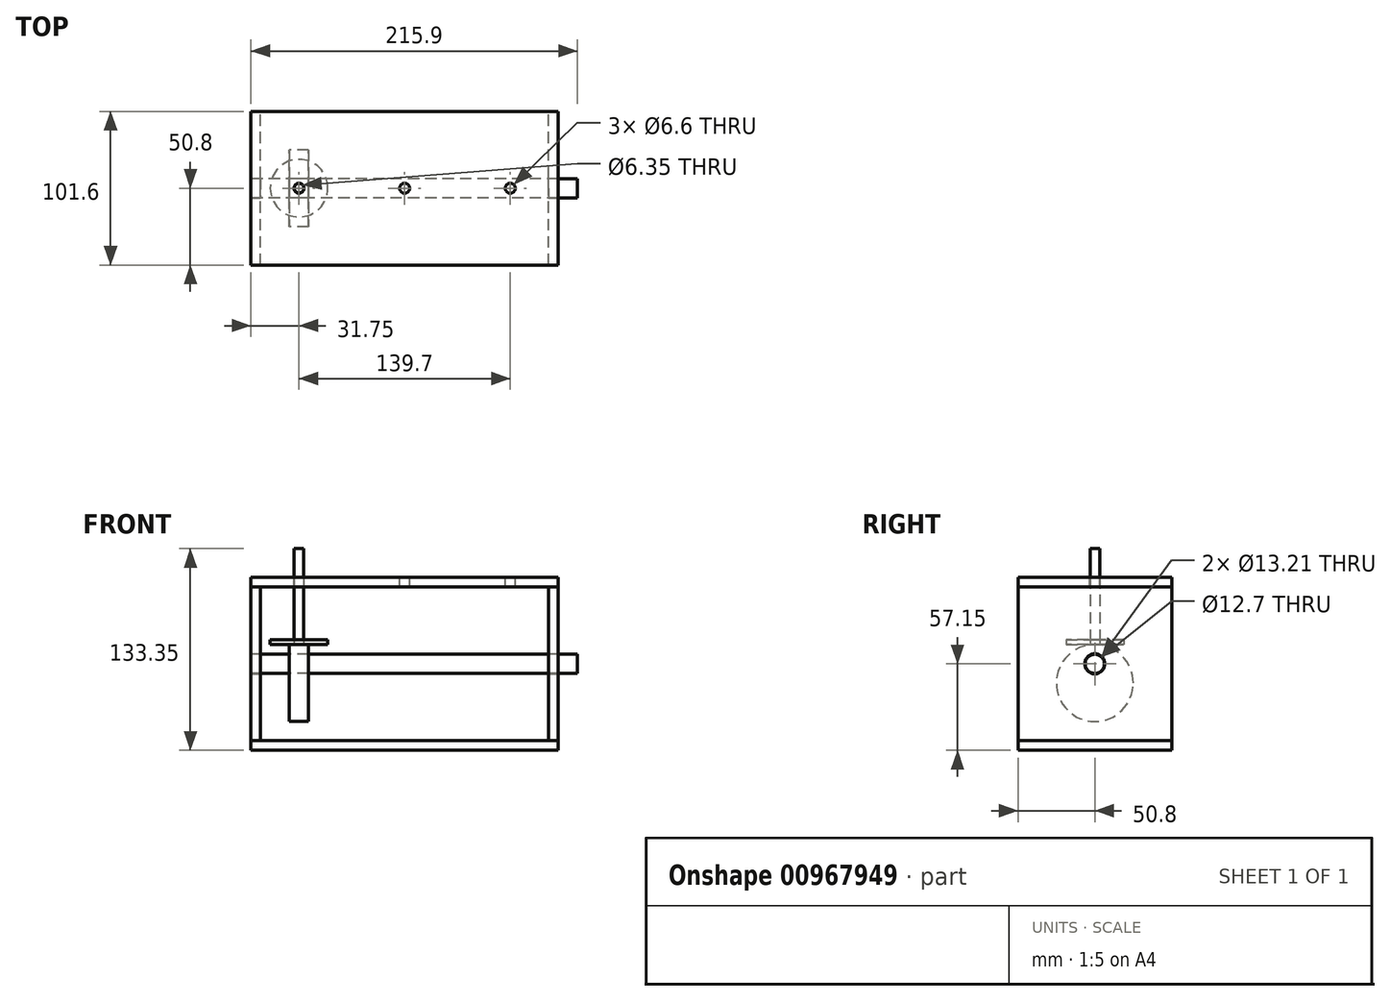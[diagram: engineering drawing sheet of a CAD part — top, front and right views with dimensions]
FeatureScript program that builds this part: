
annotation { "Feature Type Name" : "Feature", "Feature Type Description" : "" }
export const myFeature = defineFeature(function(context is Context, id is Id, definition is map)
    precondition{}
    {
        {
            assignVariable(context, id + "F0", {"name" : "thickness", "anyValue" : 101.6 * mm});
        }
        {
            var Q0;
            Q0=qCreatedBy(makeId("Front.planeOp"),FACE);
            var sketch = newSketch(context, id + "F1", { "sketchPlane" : qUnion([Q0])});
            skLineSegment(sketch, "E0.bottom", {"start": v(-101.6, 6.35) * mm, "end": v(101.6, 6.35) * mm});
            skLineSegment(sketch, "E0.top", {"start": v(-101.6, 0) * mm, "end": v(101.6, 0) * mm});
            skLineSegment(sketch, "E0.left", {"start": v(-101.6, 6.35) * mm, "end": v(-101.6, 0) * mm});
            skLineSegment(sketch, "E0.right", {"start": v(101.6, 6.35) * mm, "end": v(101.6, 0) * mm});
            skLineSegment(sketch, "E1", {"start": v(-101.6, 6.35) * mm, "end": v(-101.6, 107.95) * mm});
            skLineSegment(sketch, "E2", {"start": v(-101.6, 107.95) * mm, "end": v(101.6, 107.95) * mm});
            skLineSegment(sketch, "E3", {"start": v(101.6, 107.95) * mm, "end": v(101.6, 6.35) * mm});
            skLineSegment(sketch, "E4", {"start": v(-95.25, 6.35) * mm, "end": v(-95.25, 107.95) * mm});
            skLineSegment(sketch, "E5", {"start": v(95.25, 6.35) * mm, "end": v(95.25, 107.95) * mm});
            skLineSegment(sketch, "E6", {"start": v(-95.25, 57.15) * mm, "end": v(-101.6, 57.15) * mm, "construction": true});
            skLineSegment(sketch, "E7", {"start": v(95.25, 57.15) * mm, "end": v(101.6, 57.15) * mm, "construction": true});
            skLineSegment(sketch, "E8", {"start": v(-101.6, 107.95) * mm, "end": v(-101.6, 114.3) * mm});
            skLineSegment(sketch, "E9", {"start": v(-101.6, 114.3) * mm, "end": v(101.6, 114.3) * mm});
            skLineSegment(sketch, "E10", {"start": v(101.6, 114.3) * mm, "end": v(101.6, 107.95) * mm});
            skLineSegment(sketch, "E11", {"start": v(-95.25, 57.15) * mm, "end": v(-69.85, 57.15) * mm});
            skLineSegment(sketch, "E12", {"start": v(-69.85, 57.15) * mm, "end": v(0, 57.15) * mm});
            skLineSegment(sketch, "E13", {"start": v(0, 57.15) * mm, "end": v(69.85, 57.15) * mm});
            skLineSegment(sketch, "E14", {"start": v(69.85, 57.15) * mm, "end": v(95.25, 57.15) * mm});
            skLineSegment(sketch, "E15", {"start": v(-69.85, 57.15) * mm, "end": v(-69.85, 44.45) * mm, "construction": true});
            skLineSegment(sketch, "E16", {"start": v(0, 63.5) * mm, "end": v(0, 57.15) * mm, "construction": true});
            skLineSegment(sketch, "E17", {"start": v(69.85, 57.15) * mm, "end": v(69.85, 63.5) * mm, "construction": true});
            skLineSegment(sketch, "E18.bottom", {"start": v(-63.5, 69.85) * mm, "end": v(-76.2, 69.85) * mm});
            skLineSegment(sketch, "E18.top", {"start": v(-63.5, 19.05) * mm, "end": v(-76.2, 19.05) * mm});
            skLineSegment(sketch, "E18.left", {"start": v(-63.5, 69.85) * mm, "end": v(-63.5, 19.05) * mm});
            skLineSegment(sketch, "E18.right", {"start": v(-76.2, 69.85) * mm, "end": v(-76.2, 19.05) * mm});
            skPoint(sketch, "E18.middle", {"position": v(-69.85, 44.45) * mm});
            skLineSegment(sketch, "E19.bottom", {"start": v(6.35, 38.1) * mm, "end": v(-6.35, 38.1) * mm});
            skLineSegment(sketch, "E19.top", {"start": v(6.35, 88.9) * mm, "end": v(-6.35, 88.9) * mm});
            skLineSegment(sketch, "E19.left", {"start": v(6.35, 38.1) * mm, "end": v(6.35, 88.9) * mm});
            skLineSegment(sketch, "E19.right", {"start": v(-6.35, 38.1) * mm, "end": v(-6.35, 88.9) * mm});
            skPoint(sketch, "E19.middle", {"position": v(0, 63.5) * mm});
            skLineSegment(sketch, "E20.bottom", {"start": v(63.5, 38.1) * mm, "end": v(76.2, 38.1) * mm});
            skLineSegment(sketch, "E20.top", {"start": v(63.5, 88.9) * mm, "end": v(76.2, 88.9) * mm});
            skLineSegment(sketch, "E20.left", {"start": v(63.5, 38.1) * mm, "end": v(63.5, 88.9) * mm});
            skLineSegment(sketch, "E20.right", {"start": v(76.2, 38.1) * mm, "end": v(76.2, 88.9) * mm});
            skPoint(sketch, "E20.middle", {"position": v(69.85, 63.5) * mm});
            skLineSegment(sketch, "E21", {"start": v(-76.2, 44.45) * mm, "end": v(-63.5, 44.45) * mm});
            skLineSegment(sketch, "E22", {"start": v(-6.35, 63.5) * mm, "end": v(6.35, 63.5) * mm});
            skLineSegment(sketch, "E23", {"start": v(63.5, 63.5) * mm, "end": v(76.2, 63.5) * mm});
            skLineSegment(sketch, "E24", {"start": v(-69.85, 69.85) * mm, "end": v(-69.85, 133.35) * mm, "construction": true});
            skLineSegment(sketch, "E25", {"start": v(0, 88.9) * mm, "end": v(0, 152.4) * mm, "construction": true});
            skLineSegment(sketch, "E26", {"start": v(69.85, 88.9) * mm, "end": v(69.85, 152.4) * mm, "construction": true});
            skSolve(sketch);
        }
        {
            var Q0;
            Q0=makeQuery(id+"F1.imprint","IMPRINT",FACE,{"disambiguationData":[TD([[makeQuery(id+"F1.imprint","IMPRINT",EDGE,{"derivedFrom":sQuery(id+"F1.wireOp",EDGE,"E0.top")}),1.0]])]});
            var Q1;
            {var subQ0=sQuery(id+"F1.wireOp",EDGE,"E8");Q1=makeQuery(id+"F1.imprint","IMPRINT",FACE,{"disambiguationData":[TD([[makeQuery(id+"F1.imprint","IMPRINT",EDGE,{"derivedFrom":subQ0}),-1.0]])]});}
            extrude(context, id + "F2", {"entities" : qUnion([Q0, Q1]), "endBound" : BoundingType.SYMMETRIC, "depth" : getVariable(context, 'thickness'), "offsetDistance" : 25.4 * mm});
        }
        {
            var Q0;
            {var subQ1=sQuery(id+"F1.wireOp",EDGE,"E1");Q0=makeQuery(id+"F1.imprint","IMPRINT",FACE,{"disambiguationData":[TD([[makeQuery(id+"F1.imprint","IMPRINT",EDGE,{"derivedFrom":subQ1}),-1.0]])]});}
            var Q1;
            {var subQ4=sQuery(id+"F1.wireOp",EDGE,"E3");Q1=makeQuery(id+"F1.imprint","IMPRINT",FACE,{"disambiguationData":[TD([[makeQuery(id+"F1.imprint","IMPRINT",EDGE,{"derivedFrom":subQ4}),-1.0]])]});}
            var Q2;
            Q2=makeQuery(id+"F2.opExtrude","CAP_FACE",FACE,{"disambiguationData":[OSD([sQuery(id+"F1.wireOp",EDGE,"E2"),sQuery(id+"F1.wireOp",EDGE,"E8"),sQuery(id+"F1.wireOp",EDGE,"E9"),sQuery(id+"F1.wireOp",EDGE,"E10")])],"isStart":false});
            var Q3;
            Q3=makeQuery(id+"F2.opExtrude","CAP_FACE",FACE,{"disambiguationData":[OSD([sQuery(id+"F1.wireOp",EDGE,"E2"),sQuery(id+"F1.wireOp",EDGE,"E8"),sQuery(id+"F1.wireOp",EDGE,"E9"),sQuery(id+"F1.wireOp",EDGE,"E10")])],"isStart":true});
            extrude(context, id + "F3", {"entities" : qUnion([Q0, Q1]), "endBound" : BoundingType.UP_TO_SURFACE, "depth" : 25.4 * mm, "endBoundEntityFace" : qUnion([Q2]), "offsetDistance" : 25.4 * mm, "hasSecondDirection" : true, "secondDirectionBound" : SecondDirectionBoundingType.UP_TO_SURFACE, "secondDirectionOppositeDirection" : true, "secondDirectionDepth" : 25.4 * mm, "secondDirectionBoundEntityFace" : qUnion([Q3])});
        }
        {
            var Q0;
            Q0=makeQuery(id+"F3.opExtrude","SWEPT_FACE",FACE,{"disambiguationData":[OSD([sQuery(id+"F1.wireOp",EDGE,"E3")])]});
            var sketch = newSketch(context, id + "F4", { "sketchPlane" : qUnion([Q0])});
            skCircle(sketch, "E27", {"center": v(0, 57.15) * mm, "radius": 6.6 * mm});
            skCircle(sketch, "E28", {"center": v(0, 57.15) * mm, "radius": 6.35 * mm});
            skSolve(sketch);
        }
        {
            var Q0;
            Q0=makeQuery(id+"F4.imprint","IMPRINT",FACE,{"disambiguationData":[TD([[makeQuery(id+"F4.imprint","IMPRINT",EDGE,{"derivedFrom":sQuery(id+"F4.wireOp",EDGE,"E28")}),1.0]])]});
            var Q1;
            Q1=makeQuery(id+"F4.imprint","IMPRINT",FACE,{"disambiguationData":[TD([[makeQuery(id+"F4.imprint","IMPRINT",EDGE,{"derivedFrom":sQuery(id+"F4.wireOp",EDGE,"E27")}),1.0]])]});
            extrude(context, id + "F5", {"entities" : qUnion([Q0, Q1]), "operationType" : NewBodyOperationType.REMOVE, "endBound" : BoundingType.THROUGH_ALL, "oppositeDirection" : true, "depth" : 25.4 * mm, "offsetDistance" : 25.4 * mm});
        }
        {
            var Q0;
            Q0=makeQuery(id+"F4.imprint","IMPRINT",FACE,{"disambiguationData":[TD([[makeQuery(id+"F4.imprint","IMPRINT",EDGE,{"derivedFrom":sQuery(id+"F4.wireOp",EDGE,"E28")}),1.0]])]});
            var Q1;
            Q1=makeQuery(id+"F3.opExtrude","SWEPT_FACE",FACE,{"disambiguationData":[OSD([sQuery(id+"F1.wireOp",EDGE,"E1")])]});
            extrude(context, id + "F6", {"entities" : qUnion([Q0]), "depth" : 12.7 * mm, "offsetDistance" : 25.4 * mm, "hasSecondDirection" : true, "secondDirectionBound" : SecondDirectionBoundingType.UP_TO_SURFACE, "secondDirectionOppositeDirection" : true, "secondDirectionDepth" : 25.4 * mm, "secondDirectionBoundEntityFace" : qUnion([Q1])});
        }
        {
            var Q0;
            {var subQ0=sQuery(id+"F1.wireOp",EDGE,"E18.top");Q0=makeQuery(id+"F1.imprint","IMPRINT",FACE,{"disambiguationData":[TD([[makeQuery(id+"F1.imprint","IMPRINT",EDGE,{"derivedFrom":subQ0}),-1.0]])]});}
            var Q1;
            Q1=sQuery(id+"F1.wireOp",EDGE,"E21");
            revolve(context, id + "F7", {"surfaceOperationType" : NewSurfaceOperationType.NEW, "entities" : qUnion([Q0]), "axis" : qUnion([Q1]), "revolveType" : RevolveType.FULL});
        }
        {
            var Q0;
            Q0=makeQuery(id+"F6.opExtrude","SWEPT_BODY",BODY,{"disambiguationData":[OSD([sQuery(id+"F4.wireOp",EDGE,"E28")])]});
            var Q1;
            Q1=makeQuery(id+"F7.opRevolve","SWEPT_BODY",BODY,{"disambiguationData":[OSD([sQuery(id+"F1.wireOp",EDGE,"E18.top"),sQuery(id+"F1.wireOp",EDGE,"E18.left"),sQuery(id+"F1.wireOp",EDGE,"E18.right"),sQuery(id+"F1.wireOp",EDGE,"E21")])]});
            booleanBodies(context, id + "F8", {"operationType" : BooleanOperationType.SUBTRACTION, "tools" : qUnion([Q0]), "targets" : qUnion([Q1]), "keepTools" : true});
        }
        {
            var Q0;
            Q0=makeQuery(id+"F2.opExtrude","SWEPT_FACE",FACE,{"disambiguationData":[OSD([sQuery(id+"F1.wireOp",EDGE,"E9")])]});
            var sketch = newSketch(context, id + "F9", { "sketchPlane" : qUnion([Q0])});
            skPoint(sketch, "E29", {"position": v(0, 0) * mm});
            skPoint(sketch, "E30", {"position": v(-69.85, 0) * mm});
            skPoint(sketch, "E31", {"position": v(69.85, 0) * mm});
            skSolve(sketch);
        }
        {
            var Q0;
            Q0=sQuery(id+"F9.wireOp",VERTEX,"E30");
            var Q1;
            Q1=sQuery(id+"F9.wireOp",VERTEX,"E29");
            var Q2;
            Q2=sQuery(id+"F9.wireOp",VERTEX,"E31");
            var Q3;
            Q3=makeQuery(id+"F2.opExtrude","SWEPT_BODY",BODY,{"disambiguationData":[OSD([sQuery(id+"F1.wireOp",EDGE,"E2"),sQuery(id+"F1.wireOp",EDGE,"E8"),sQuery(id+"F1.wireOp",EDGE,"E9"),sQuery(id+"F1.wireOp",EDGE,"E10")])]});
            hole(context, id + "F10", {"style" : HoleStyle.SIMPLE, "endStyle" : HoleEndStyle.THROUGH, "holeDiameter" : 6.6 * mm, "majorDiameter" : 6.35 * mm, "isTappedThrough" : true, "tappedDepth" : 12.7 * mm, "tapClearance" : 3, "locations" : qUnion([Q0, Q1, Q2]), "scope" : qUnion([Q3])});
        }
        {
            var Q0;
            Q0=sQuery(id+"F1.wireOp",VERTEX,"E24.start");
            var Q1;
            Q1=qCreatedBy(makeId("Top.planeOp"),FACE);
            cPlane(context, id + "F11", {"entities" : qUnion([Q0, Q1]), "cplaneType" : CPlaneType.PLANE_POINT, "offset" : 25.4 * mm, "width" : 152.4 * mm, "height" : 152.4 * mm});
        }
        {
            var Q0;
            Q0=qCreatedBy(id+"F11.planeOp",FACE);
            var sketch = newSketch(context, id + "F12", { "sketchPlane" : qUnion([Q0])});
            skCircle(sketch, "E32", {"center": v(-69.85, 0) * mm, "radius": 3.18 * mm});
            skCircle(sketch, "E33", {"center": v(-69.85, 0) * mm, "radius": 19.05 * mm});
            skSolve(sketch);
        }
        {
            var Q0;
            Q0=makeQuery(id+"F12.imprint","IMPRINT",FACE,{"disambiguationData":[TD([[makeQuery(id+"F12.imprint","IMPRINT",EDGE,{"derivedFrom":sQuery(id+"F12.wireOp",EDGE,"E32")}),1.0]])]});
            var Q1;
            Q1=sQuery(id+"F1.wireOp",VERTEX,"E24.end");
            extrude(context, id + "F13", {"entities" : qUnion([Q0]), "endBound" : BoundingType.UP_TO_VERTEX, "depth" : 25.4 * mm, "endBoundEntityVertex" : qUnion([Q1]), "offsetDistance" : 25.4 * mm});
        }
        {
            var Q0;
            Q0=makeQuery(id+"F12.imprint","IMPRINT",FACE,{"disambiguationData":[TD([[makeQuery(id+"F12.imprint","IMPRINT",EDGE,{"derivedFrom":sQuery(id+"F12.wireOp",EDGE,"E32")}),-1.0]])]});
            extrude(context, id + "F14", {"entities" : qUnion([Q0]), "depth" : 3.17 * mm, "offsetDistance" : 25.4 * mm});
        }
    });
